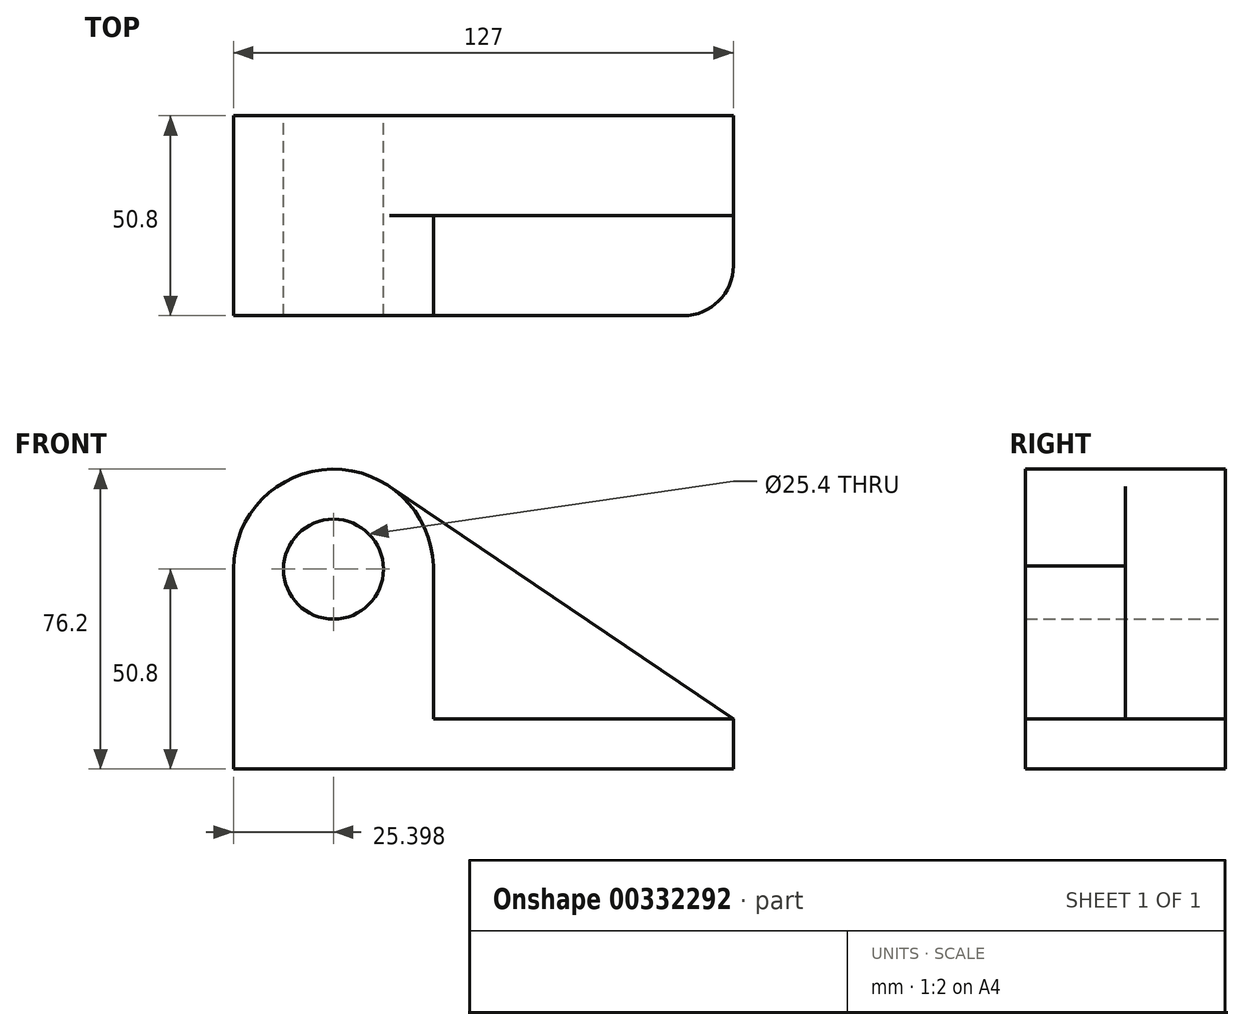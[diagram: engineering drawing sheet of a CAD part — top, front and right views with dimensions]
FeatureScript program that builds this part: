
annotation { "Feature Type Name" : "Feature", "Feature Type Description" : "" }
export const myFeature = defineFeature(function(context is Context, id is Id, definition is map)
    precondition{}
    {
        {
            var Q0;
            Q0=qCreatedBy(makeId("Front.planeOp"),FACE);
            var sketch = newSketch(context, id + "F0", { "sketchPlane" : qUnion([Q0])});
            skCircle(sketch, "E0", {"center": v(-42.06, 38.1) * mm, "radius": 12.7 * mm});
            skArc(sketch, "E1", {"start": v(-27.82, 59.13) * mm, "mid": v(-53.97, 60.54) * mm, "end": v(-67.46, 38.1) * mm});
            skLineSegment(sketch, "E2", {"start": v(-67.46, 38.1) * mm, "end": v(-67.46, -12.7) * mm});
            skLineSegment(sketch, "E3", {"start": v(-67.46, -12.7) * mm, "end": v(59.54, -12.7) * mm});
            skLineSegment(sketch, "E4", {"start": v(59.54, -12.7) * mm, "end": v(59.54, 0) * mm});
            skLineSegment(sketch, "E5", {"start": v(59.54, 0) * mm, "end": v(-27.82, 59.13) * mm});
            skSolve(sketch);
        }
        {
            var Q0;
            Q0 = qSketchRegion(id + "F0", true);
            extrude(context, id + "F1", {"entities" : qUnion([Q0]), "depth" : 25.4 * mm});
        }
        {
            var Q0;
            Q0=makeQuery(id+"F1.opExtrude","CAP_FACE",FACE,{"disambiguationData":[OSD([sQuery(id+"F0.wireOp",EDGE,"E0"),sQuery(id+"F0.wireOp",EDGE,"E1"),sQuery(id+"F0.wireOp",EDGE,"E2"),sQuery(id+"F0.wireOp",EDGE,"E3"),sQuery(id+"F0.wireOp",EDGE,"E4"),sQuery(id+"F0.wireOp",EDGE,"E5")])],"isStart":false});
            var sketch = newSketch(context, id + "F2", { "sketchPlane" : qUnion([Q0])});
            skCircle(sketch, "E6", {"center": v(-42.06, 38.1) * mm, "radius": 12.7 * mm});
            skArc(sketch, "E7", {"start": v(-16.67, 37.31) * mm, "mid": v(-41.67, 63.5) * mm, "end": v(-67.46, 38.1) * mm});
            skLineSegment(sketch, "E8.bottom", {"start": v(59.54, 0) * mm, "end": v(-16.67, 0) * mm});
            skLineSegment(sketch, "E8.top", {"start": v(59.54, 0) * mm, "end": v(-16.67, 0) * mm});
            skLineSegment(sketch, "E8.left", {"start": v(59.54, 0) * mm, "end": v(59.54, 0) * mm});
            skLineSegment(sketch, "E8.right", {"start": v(-67.46, 0) * mm, "end": v(-67.46, 0) * mm});
            skLineSegment(sketch, "E9", {"start": v(-67.46, 38.1) * mm, "end": v(-67.46, 0) * mm});
            skLineSegment(sketch, "E10", {"start": v(-16.67, 38.89) * mm, "end": v(-16.67, 0) * mm});
            skSolve(sketch);
        }
        {
            var Q0;
            Q0=makeQuery(id+"F2.imprint","IMPRINT",FACE,{"disambiguationData":[TD([[makeQuery(id+"F2.imprint","IMPRINT",EDGE,{"derivedFrom":sQuery(id+"F2.wireOp",EDGE,"E6")}),-1.0]])]});
            extrude(context, id + "F3", {"entities" : qUnion([Q0]), "operationType" : NewBodyOperationType.ADD, "depth" : 25.4 * mm});
        }
        {
            var Q0;
            Q0=makeQuery(id+"F3.opExtrude","CAP_EDGE",EDGE,{"disambiguationData":[OSD([sQuery(id+"F0.wireOp",EDGE,"E4")])],"isStart":false});
            fillet(context, id + "F4", {"entities" : qUnion([Q0]), "radius" : 12.7 * mm, "tangentPropagation" : true, "allowEdgeOverflow" : false});
        }
    });
